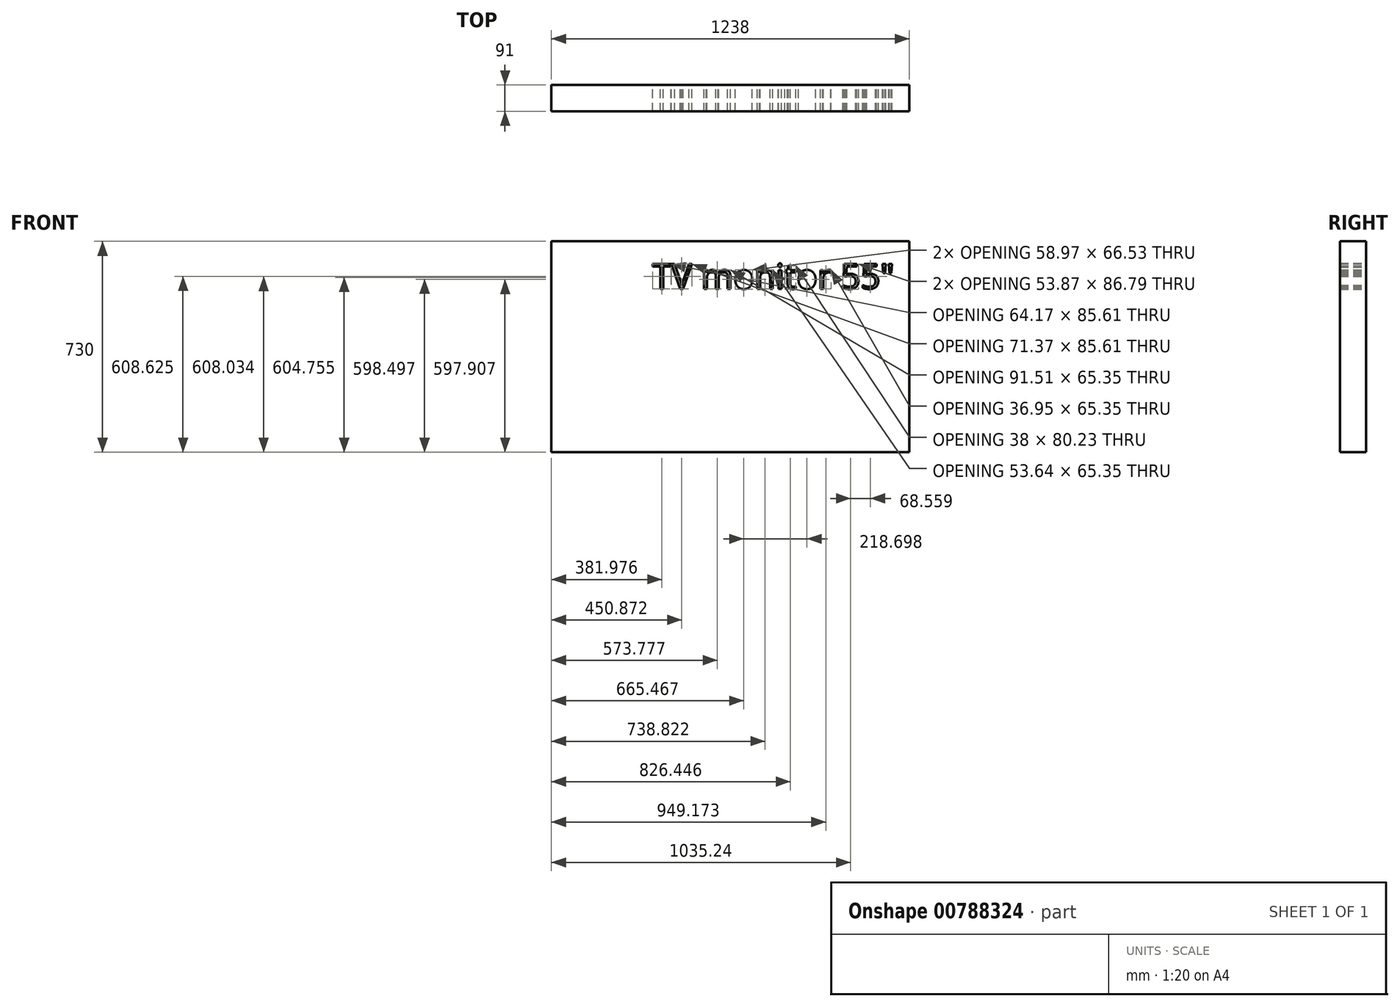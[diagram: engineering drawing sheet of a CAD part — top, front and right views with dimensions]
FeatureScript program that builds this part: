
annotation { "Feature Type Name" : "Feature", "Feature Type Description" : "" }
export const myFeature = defineFeature(function(context is Context, id is Id, definition is map)
    precondition{}
    {
        {
            var Q0;
            Q0=qCreatedBy(makeId("Front.planeOp"),FACE);
            var sketch = newSketch(context, id + "F0", { "sketchPlane" : qUnion([Q0])});
            skLineSegment(sketch, "E0.bottom", {"start": v(619, -365) * mm, "end": v(-619, -365) * mm});
            skLineSegment(sketch, "E0.top", {"start": v(619, 365) * mm, "end": v(-619, 365) * mm});
            skLineSegment(sketch, "E0.left", {"start": v(619, -365) * mm, "end": v(619, 365) * mm});
            skLineSegment(sketch, "E0.right", {"start": v(-619, -365) * mm, "end": v(-619, 365) * mm});
            skPoint(sketch, "E0.middle", {"position": v(0, 0) * mm});
            skText(sketch, "E1", { "text": "TV monitor 55\"", "fontName": "OpenSans-Regular.ttf"});
            const initialGuessF0  = {"E1": [-0.27016, 0.20082, 1, 0, 0.08634]};
            skSetInitialGuess(sketch, initialGuessF0);
            skSolve(sketch);
        }
        {
            var Q0;
            Q0=makeQuery(id+"F0.imprint","IMPRINT",FACE,{"disambiguationData":[TD([[makeQuery(id+"F0.imprint","IMPRINT",EDGE,{"derivedFrom":sQuery(id+"F0.wireOp",EDGE,"E0.bottom")}),-1.0]])]});
            extrude(context, id + "F1", {"entities" : qUnion([Q0]), "depth" : 91 * mm, "offsetDistance" : 25 * mm});
        }
    });
